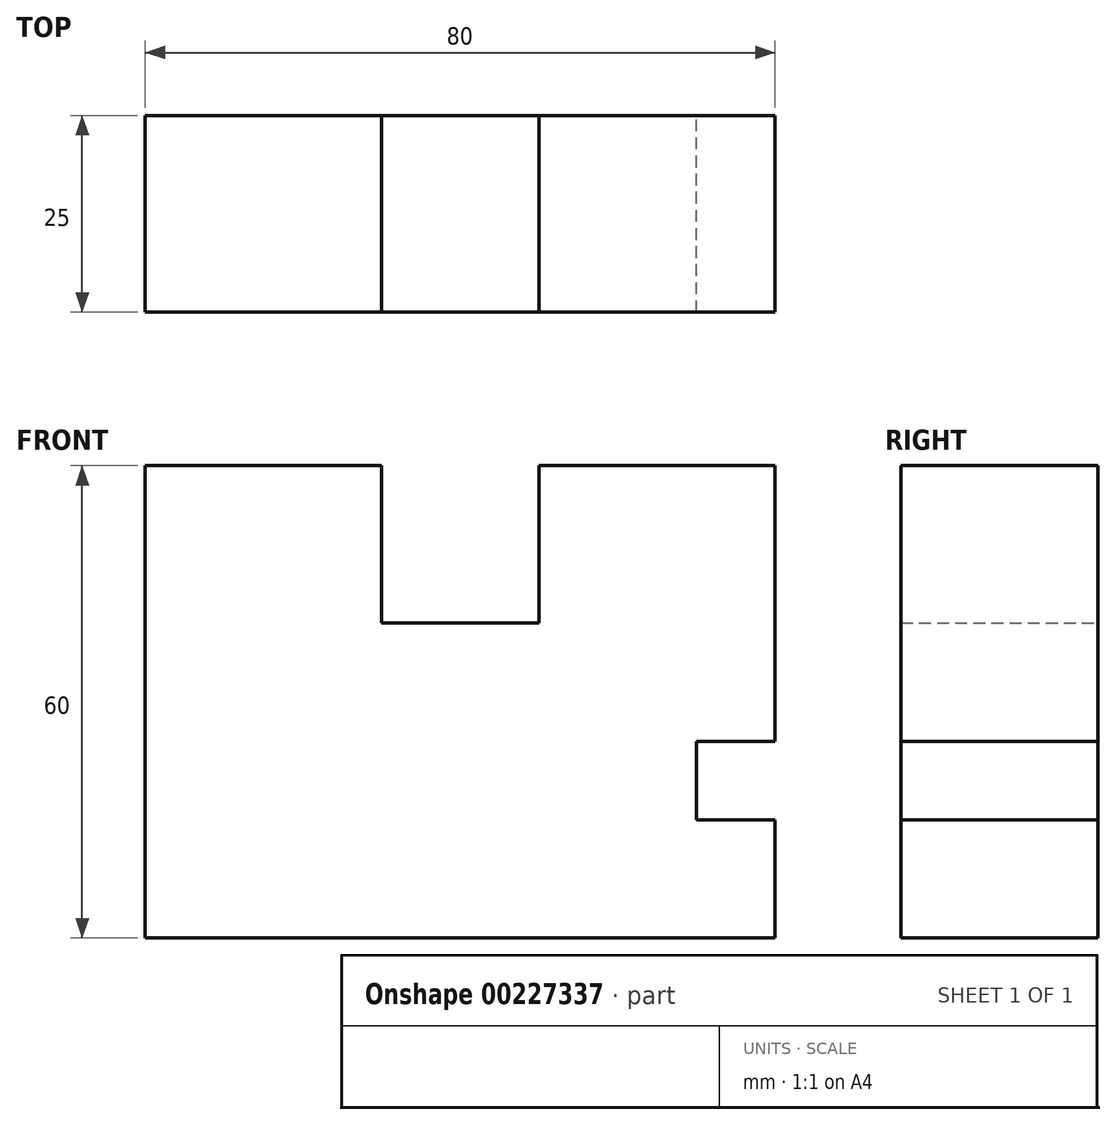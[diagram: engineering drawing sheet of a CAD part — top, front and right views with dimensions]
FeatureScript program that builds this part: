
annotation { "Feature Type Name" : "Feature", "Feature Type Description" : "" }
export const myFeature = defineFeature(function(context is Context, id is Id, definition is map)
    precondition{}
    {
        {
            var Q0;
            Q0=qCreatedBy(makeId("Front.planeOp"),FACE);
            var sketch = newSketch(context, id + "F0", { "sketchPlane" : qUnion([Q0])});
            skLineSegment(sketch, "E0", {"start": v(-80, 60) * mm, "end": v(-80, 0) * mm});
            skLineSegment(sketch, "E1", {"start": v(-80, 0) * mm, "end": v(0, 0) * mm});
            skLineSegment(sketch, "E2", {"start": v(0, 0) * mm, "end": v(0, 15) * mm});
            skLineSegment(sketch, "E3", {"start": v(0, 25) * mm, "end": v(0, 60) * mm});
            skLineSegment(sketch, "E4", {"start": v(0, 60) * mm, "end": v(-30, 60) * mm});
            skLineSegment(sketch, "E5", {"start": v(-30, 60) * mm, "end": v(-30, 40) * mm});
            skLineSegment(sketch, "E6", {"start": v(-30, 40) * mm, "end": v(-50, 40) * mm});
            skLineSegment(sketch, "E7", {"start": v(-50, 40) * mm, "end": v(-50, 60) * mm});
            skLineSegment(sketch, "E8", {"start": v(0, 25) * mm, "end": v(-10, 25) * mm});
            skLineSegment(sketch, "E9", {"start": v(-10, 15) * mm, "end": v(-10, 25) * mm});
            skLineSegment(sketch, "E10", {"start": v(-10, 15) * mm, "end": v(0, 15) * mm});
            skLineSegment(sketch, "E11", {"start": v(-80, 60) * mm, "end": v(-50, 60) * mm});
            skLineSegment(sketch, "E12", {"start": v(0, 0) * mm, "end": v(0, -60) * mm});
            skLineSegment(sketch, "E13", {"start": v(0, -60) * mm, "end": v(60, -60) * mm});
            skLineSegment(sketch, "E14", {"start": v(10, -50) * mm, "end": v(10, -10) * mm});
            skLineSegment(sketch, "E15", {"start": v(10, -10) * mm, "end": v(25, -10) * mm});
            skLineSegment(sketch, "E16", {"start": v(25, -10) * mm, "end": v(15, 0) * mm});
            skLineSegment(sketch, "E17", {"start": v(15, 0) * mm, "end": v(0, 0) * mm});
            skLineSegment(sketch, "E18", {"start": v(55, -50) * mm, "end": v(60, -60) * mm});
            skLineSegment(sketch, "E19", {"start": v(10, -50) * mm, "end": v(55, -50) * mm});
            skSolve(sketch);
        }
        {
            var Q0;
            Q0=makeQuery(id+"F0.imprint","IMPRINT",FACE,{"disambiguationData":[TD([[makeQuery(id+"F0.imprint","IMPRINT",EDGE,{"derivedFrom":sQuery(id+"F0.wireOp",EDGE,"E0")}),1.0]])]});
            extrude(context, id + "F1", {"entities" : qUnion([Q0]), "depth" : 25 * mm});
        }
    });
